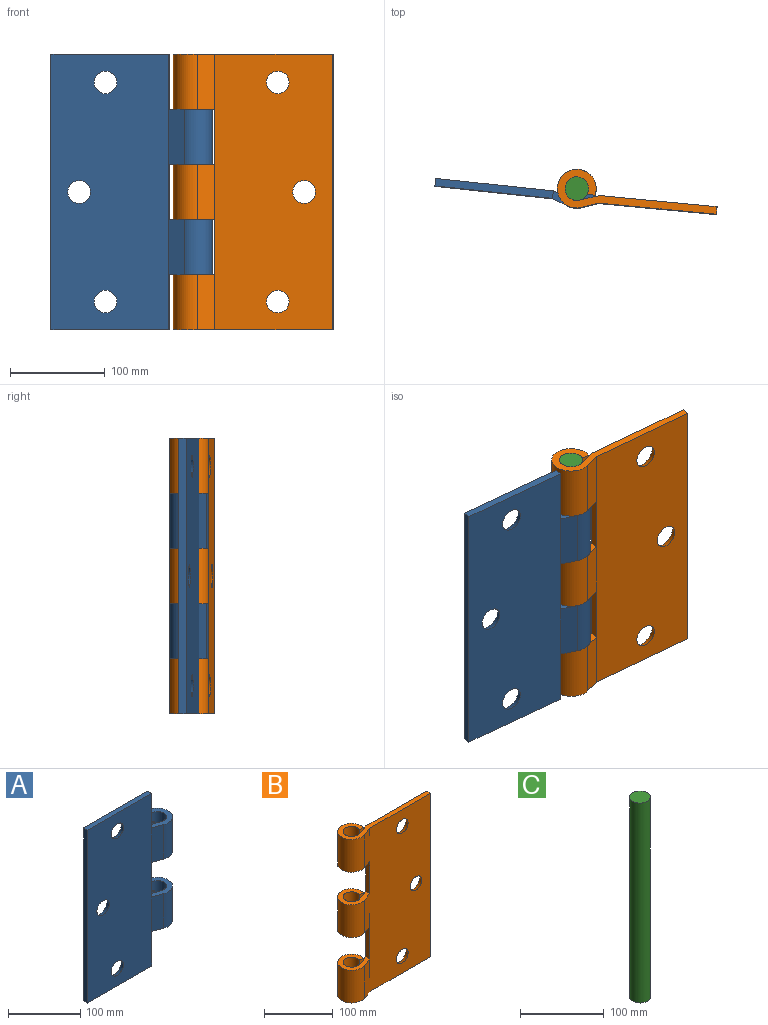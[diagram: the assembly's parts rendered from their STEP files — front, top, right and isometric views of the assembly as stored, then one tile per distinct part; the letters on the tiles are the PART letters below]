
ASSEMBLY  parts=3 mates=2
PART A: 25 faces, bbox 170x41x292 mm
  f0: plane 58.4x20.54mm, normal (0.32,0.95,0), area 1264.7mm2, adj f8,f12,f20,f22
  f1: plane 58.4x20.54mm, normal (0.32,0.95,0), area 1264.7mm2, adj f9,f12,f19,f24
  f2: plane 58.4x17.59mm, normal (-0.34,-0.94,0), area 1091mm2, adj f4,f14,f20,f22
  f3: plane 58.4x17.59mm, normal (-0.34,-0.94,0), area 1091mm2, adj f5,f14,f19,f24
  f4: cylinder r=20.5mm len=58.4mm, axis (0,0,-1), area 6348.4mm2, adj f2,f6,f20,f22
  f5: cylinder r=20.5mm len=58.4mm, axis (0,0,-1), area 6348.4mm2, adj f3,f7,f19,f24
  f6: plane 58.4x8.42mm, normal (0,-1,0), area 492mm2, adj f4,f8,f20,f22
  f7: plane 58.4x8.42mm, normal (0,-1,0), area 492mm2, adj f5,f9,f19,f24
  f8: cylinder r=12.5mm len=58.4mm, axis (0,0,-1), area 3975.6mm2, adj f0,f6,f20,f22
  f9: cylinder r=12.5mm len=58.4mm, axis (0,0,-1), area 3975.6mm2, adj f1,f7,f19,f24
  f10: plane 125x8mm, normal (0,0,1), area 1000mm2, adj f12,f13,f14,f21
  f11: plane 125x8mm, normal (0,0,-1), area 1000mm2, adj f12,f13,f14,f23
  f12: plane 292x125mm, normal (0,1,0), area 34087.3mm2, adj f0,f1,f10,f11,f13,f15,f16,f17
  f13: plane 292x8mm, normal (-1,0,0), area 2336mm2, adj f10,f11,f12,f14
  f14: plane 292x125mm, normal (0,-1,0), area 35142.8mm2, adj f2,f3,f10,f11,f13,f15,f16,f17
  f15: cone r=12mm half-angle=26.6deg, axis (0,1,0), area 786.8mm2, adj f12,f14
  f16: cone r=12mm half-angle=26.6deg, axis (0,1,0), area 786.8mm2, adj f12,f14
  f17: cone r=12mm half-angle=26.6deg, axis (0,1,0), area 786.8mm2, adj f12,f14
  f18: plane 58.4x8mm, normal (1,0,0), area 467.2mm2, adj f12,f14,f19,f20
  f19: plane 45x41mm, normal (0,0,1), area 864mm2, adj f1,f3,f5,f7,f9,f18
  f20: plane 45x41mm, normal (0,0,-1), area 864mm2, adj f0,f2,f4,f6,f8,f18
  f21: plane 58.4x8mm, normal (1,0,0), area 467.2mm2, adj f10,f12,f14,f22
  f22: plane 45x41mm, normal (0,0,1), area 864mm2, adj f0,f2,f4,f6,f8,f21
  f23: plane 58.4x8mm, normal (1,0,0), area 467.2mm2, adj f11,f12,f14,f24
  f24: plane 45x41mm, normal (0,0,-1), area 864mm2, adj f1,f3,f5,f7,f9,f23
PART B: 29 faces, bbox 170x41x292 mm
  f0: plane 58.4x20.54mm, normal (-0.32,0.95,0), area 1264.7mm2, adj f8,f11,f25,f27
  f1: plane 58.4x20.54mm, normal (-0.32,0.95,0), area 1264.7mm2, adj f9,f11,f18,f24
  f2: plane 58.4x17.59mm, normal (0.34,-0.94,0), area 1091mm2, adj f4,f13,f25,f27
  f3: plane 58.4x17.59mm, normal (0.34,-0.94,0), area 1091mm2, adj f5,f13,f18,f24
  f4: cylinder r=20.5mm len=58.4mm, axis (0,0,-1), area 6348.4mm2, adj f2,f6,f25,f27
  f5: cylinder r=20.5mm len=58.4mm, axis (0,0,-1), area 6348.4mm2, adj f3,f7,f18,f24
  f6: plane 58.4x8.42mm, normal (0,-1,0), area 492mm2, adj f4,f8,f25,f27
  f7: plane 58.4x8.42mm, normal (0,-1,0), area 492mm2, adj f5,f9,f18,f24
  f8: cylinder r=12.5mm len=58.4mm, axis (0,0,-1), area 3975.6mm2, adj f0,f6,f25,f27
  f9: cylinder r=12.5mm len=58.4mm, axis (0,0,-1), area 3975.6mm2, adj f1,f7,f18,f24
  f10: plane 58.4x20.54mm, normal (-0.32,0.95,0), area 1264.7mm2, adj f11,f17,f19,f28
  f11: plane 292x125mm, normal (0,1,0), area 34087.3mm2, adj f0,f1,f10,f12,f18,f19,f20,f21
  f12: plane 292x8mm, normal (1,0,0), area 2336mm2, adj f11,f13,f18,f19
  f13: plane 292x125mm, normal (0,-1,0), area 35142.8mm2, adj f2,f3,f12,f14,f18,f19,f20,f21
  f14: plane 58.4x17.59mm, normal (0.34,-0.94,0), area 1091mm2, adj f13,f15,f19,f28
  f15: cylinder r=20.5mm len=58.4mm, axis (0,0,-1), area 6348.4mm2, adj f14,f16,f19,f28
  f16: plane 58.4x8.42mm, normal (0,-1,0), area 492mm2, adj f15,f17,f19,f28
  f17: cylinder r=12.5mm len=58.4mm, axis (0,0,-1), area 3975.6mm2, adj f10,f16,f19,f28
  f18: plane 170x41mm, normal (0,0,1), area 1864mm2, adj f1,f3,f5,f7,f9,f11,f12,f13
  f19: plane 170x41mm, normal (0,0,-1), area 1864mm2, adj f10,f11,f12,f13,f14,f15,f16,f17
  f20: cone r=12mm half-angle=26.6deg, axis (0,1,0), area 786.8mm2, adj f11,f13
  f21: cone r=12mm half-angle=26.6deg, axis (0,1,0), area 786.8mm2, adj f11,f13
  f22: cone r=12mm half-angle=26.6deg, axis (0,1,0), area 786.8mm2, adj f11,f13
  f23: plane 58.4x8mm, normal (-1,0,0), area 467.2mm2, adj f11,f13,f24,f25
  f24: plane 45x41mm, normal (0,0,-1), area 864mm2, adj f1,f3,f5,f7,f9,f23
  f25: plane 45x41mm, normal (0,0,1), area 864mm2, adj f0,f2,f4,f6,f8,f23
  f26: plane 58.4x8mm, normal (-1,0,0), area 467.2mm2, adj f11,f13,f27,f28
  f27: plane 45x41mm, normal (0,0,-1), area 864mm2, adj f0,f2,f4,f6,f8,f26
  f28: plane 45x41mm, normal (0,0,1), area 864mm2, adj f10,f14,f15,f16,f17,f26
PART C: 3 faces, bbox 25x25x292 mm
  f0: cylinder r=12.5mm len=292mm, axis (0,0,-1), area 22933.6mm2, adj f1,f2
  f1: plane 25x25mm, normal (0,0,1), area 490.9mm2, adj f0
  f2: plane 25x25mm, normal (0,0,-1), area 490.9mm2, adj f0
PLACE A rot(axis=(0,0,-1),6deg) t=(-1513.95,-10.88,-3.71)mm
PLACE B rot(axis=(0,0,-1),5.4deg) t=(-1763.79,12.61,-3.71)mm
PLACE C t=(-1489.06,-8.49,-3.71)mm fixed
MATE revolute A.f4 <-> B.f4  axis (0,0,-1) through (-1489.06,-8.49,229.89)mm
MATE revolute B.f4 <-> C.f0  axis (0,0,-1) through (-1489.06,-8.49,288.29)mm
